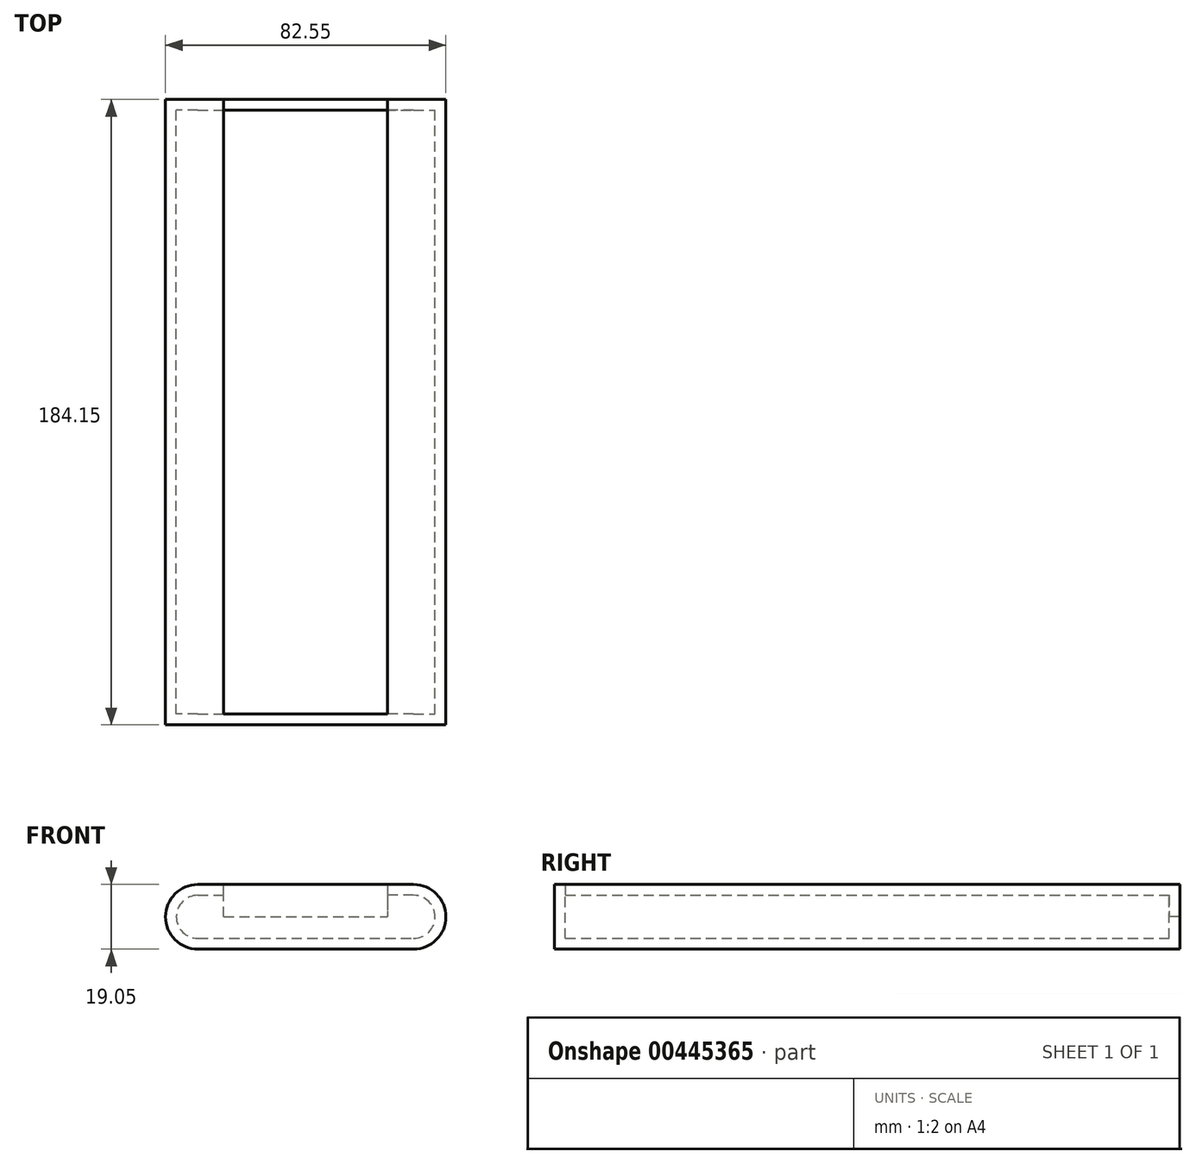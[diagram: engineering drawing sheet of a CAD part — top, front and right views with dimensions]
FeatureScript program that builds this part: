
annotation { "Feature Type Name" : "Feature", "Feature Type Description" : "" }
export const myFeature = defineFeature(function(context is Context, id is Id, definition is map)
    precondition{}
    {
        {
            var Q0;
            Q0=qCreatedBy(makeId("Front.planeOp"),FACE);
            var sketch = newSketch(context, id + "F0", { "sketchPlane" : qUnion([Q0])});
            skLineSegment(sketch, "E0", {"start": v(9.53, 0) * mm, "end": v(73.03, 0) * mm});
            skLineSegment(sketch, "E1", {"start": v(0, 9.53) * mm, "end": v(0, 9.53) * mm});
            skLineSegment(sketch, "E2", {"start": v(82.55, 9.53) * mm, "end": v(82.55, 9.53) * mm});
            skLineSegment(sketch, "E3", {"start": v(9.52, 19.05) * mm, "end": v(17.15, 19.05) * mm});
            skLineSegment(sketch, "E4", {"start": v(73.03, 19.05) * mm, "end": v(65.4, 19.05) * mm});
            skLineSegment(sketch, "E5.0", {"start": v(9.53, 3.18) * mm, "end": v(73.03, 3.18) * mm});
            skLineSegment(sketch, "E6.0", {"start": v(9.53, 15.88) * mm, "end": v(17.15, 15.88) * mm});
            skLineSegment(sketch, "E7.0", {"start": v(73.03, 15.88) * mm, "end": v(65.4, 15.88) * mm});
            skLineSegment(sketch, "E8", {"start": v(17.15, 15.88) * mm, "end": v(17.15, 19.05) * mm});
            skLineSegment(sketch, "E9", {"start": v(65.4, 19.05) * mm, "end": v(65.4, 15.87) * mm});
            skPoint(sketch, "E10.visualSharp", {"position": v(0, 19.05) * mm});
            skArc(sketch, "E10.filletArc", {"start": v(9.52, 19.05) * mm, "mid": v(2.79, 16.26) * mm, "end": v(0, 9.53) * mm});
            skPoint(sketch, "E11.visualSharp", {"position": v(0, 0) * mm});
            skArc(sketch, "E11.filletArc", {"start": v(0, 9.53) * mm, "mid": v(2.79, 2.79) * mm, "end": v(9.53, 0) * mm});
            skPoint(sketch, "E12.visualSharp", {"position": v(82.55, 19.05) * mm});
            skArc(sketch, "E12.filletArc", {"start": v(82.55, 9.53) * mm, "mid": v(79.76, 16.26) * mm, "end": v(73.03, 19.05) * mm});
            skPoint(sketch, "E13.visualSharp", {"position": v(82.55, 0) * mm});
            skArc(sketch, "E13.filletArc", {"start": v(73.03, 0) * mm, "mid": v(79.76, 2.79) * mm, "end": v(82.55, 9.53) * mm});
            skArc(sketch, "E14.0", {"start": v(79.38, 9.52) * mm, "mid": v(77.52, 14.02) * mm, "end": v(73.03, 15.87) * mm});
            skArc(sketch, "E15.0", {"start": v(73.03, 3.18) * mm, "mid": v(77.52, 5.03) * mm, "end": v(79.38, 9.53) * mm});
            skArc(sketch, "E16.0", {"start": v(9.53, 15.88) * mm, "mid": v(5.03, 14.02) * mm, "end": v(3.18, 9.53) * mm});
            skArc(sketch, "E17.0", {"start": v(3.18, 9.53) * mm, "mid": v(5.03, 5.03) * mm, "end": v(9.53, 3.18) * mm});
            skSolve(sketch);
        }
        {
            var Q0;
            Q0=makeQuery(id+"F0.imprint","IMPRINT",FACE,{"disambiguationData":[TD([[makeQuery(id+"F0.imprint","IMPRINT",EDGE,{"derivedFrom":sQuery(id+"F0.wireOp",EDGE,"E0")}),1.0]])]});
            extrude(context, id + "F1", {"entities" : qUnion([Q0]), "depth" : 177.8 * mm});
        }
        {
            var Q0;
            Q0=makeQuery(id+"F1.opExtrude","CAP_FACE",FACE,{"disambiguationData":[OSD([sQuery(id+"F0.wireOp",EDGE,"E0"),sQuery(id+"F0.wireOp",EDGE,"E3"),sQuery(id+"F0.wireOp",EDGE,"E4"),sQuery(id+"F0.wireOp",EDGE,"E5.0"),sQuery(id+"F0.wireOp",EDGE,"E6.0"),sQuery(id+"F0.wireOp",EDGE,"E7.0"),sQuery(id+"F0.wireOp",EDGE,"E8"),sQuery(id+"F0.wireOp",EDGE,"E9"),sQuery(id+"F0.wireOp",EDGE,"E10.filletArc"),sQuery(id+"F0.wireOp",EDGE,"E11.filletArc"),sQuery(id+"F0.wireOp",EDGE,"E12.filletArc"),sQuery(id+"F0.wireOp",EDGE,"E13.filletArc"),sQuery(id+"F0.wireOp",EDGE,"E14.0"),sQuery(id+"F0.wireOp",EDGE,"E15.0"),sQuery(id+"F0.wireOp",EDGE,"E16.0"),sQuery(id+"F0.wireOp",EDGE,"E17.0")])],"isStart":false});
            var sketch = newSketch(context, id + "F2", { "sketchPlane" : qUnion([Q0])});
            skLineSegment(sketch, "E18", {"start": v(9.52, 19.05) * mm, "end": v(73.03, 19.05) * mm});
            skLineSegment(sketch, "E19", {"start": v(73.03, 0) * mm, "end": v(9.52, 0) * mm});
            skLineSegment(sketch, "E20.0", {"start": v(0, 9.52) * mm, "end": v(0, 9.52) * mm});
            skPoint(sketch, "E21.visualSharp", {"position": v(0, 19.05) * mm});
            skArc(sketch, "E21.filletArc", {"start": v(9.52, 19.05) * mm, "mid": v(2.79, 16.26) * mm, "end": v(0, 9.52) * mm});
            skPoint(sketch, "E22.visualSharp", {"position": v(0, 0) * mm});
            skArc(sketch, "E22.filletArc", {"start": v(0, 9.52) * mm, "mid": v(2.79, 2.79) * mm, "end": v(9.53, 0) * mm});
            skLineSegment(sketch, "E23.0", {"start": v(82.55, 9.52) * mm, "end": v(82.55, 9.53) * mm});
            skArc(sketch, "E24.filletArc", {"start": v(82.55, 9.52) * mm, "mid": v(79.76, 16.26) * mm, "end": v(73.03, 19.05) * mm});
            skArc(sketch, "E25.filletArc", {"start": v(73.03, 0) * mm, "mid": v(79.76, 2.79) * mm, "end": v(82.55, 9.53) * mm});
            skSolve(sketch);
        }
        {
            var Q0;
            Q0 = qSketchRegion(id + "F2", true);
            extrude(context, id + "F3", {"entities" : qUnion([Q0]), "operationType" : NewBodyOperationType.ADD, "depth" : 3.17 * mm});
        }
        {
            var Q0;
            Q0=makeQuery(id+"F1.opExtrude","CAP_FACE",FACE,{"disambiguationData":[OSD([sQuery(id+"F0.wireOp",EDGE,"E0"),sQuery(id+"F0.wireOp",EDGE,"E3"),sQuery(id+"F0.wireOp",EDGE,"E4"),sQuery(id+"F0.wireOp",EDGE,"E5.0"),sQuery(id+"F0.wireOp",EDGE,"E6.0"),sQuery(id+"F0.wireOp",EDGE,"E7.0"),sQuery(id+"F0.wireOp",EDGE,"E8"),sQuery(id+"F0.wireOp",EDGE,"E9"),sQuery(id+"F0.wireOp",EDGE,"E10.filletArc"),sQuery(id+"F0.wireOp",EDGE,"E11.filletArc"),sQuery(id+"F0.wireOp",EDGE,"E12.filletArc"),sQuery(id+"F0.wireOp",EDGE,"E13.filletArc"),sQuery(id+"F0.wireOp",EDGE,"E14.0"),sQuery(id+"F0.wireOp",EDGE,"E15.0"),sQuery(id+"F0.wireOp",EDGE,"E16.0"),sQuery(id+"F0.wireOp",EDGE,"E17.0")])],"isStart":true});
            var sketch = newSketch(context, id + "F4", { "sketchPlane" : qUnion([Q0])});
            skLineSegment(sketch, "E26", {"start": v(-65.4, 19.05) * mm, "end": v(-65.4, 9.53) * mm});
            skPoint(sketch, "E26.endSnap0", {"position": v(-65.4, 17.46) * mm});
            skLineSegment(sketch, "E27", {"start": v(-17.15, 19.05) * mm, "end": v(-17.15, 9.53) * mm});
            skLineSegment(sketch, "E28", {"start": v(-17.15, 9.53) * mm, "end": v(-65.4, 9.53) * mm});
            skLineSegment(sketch, "E29", {"start": v(-76.83, 19.05) * mm, "end": v(-73.03, 19.05) * mm});
            skLineSegment(sketch, "E30", {"start": v(-17.15, 19.05) * mm, "end": v(-9.53, 19.05) * mm});
            skLineSegment(sketch, "E31", {"start": v(0, 9.53) * mm, "end": v(0, 9.53) * mm});
            skLineSegment(sketch, "E32", {"start": v(-9.52, 0) * mm, "end": v(-73.03, 0) * mm});
            skPoint(sketch, "E33.visualSharp", {"position": v(0, 19.05) * mm});
            skArc(sketch, "E33.filletArc", {"start": v(0, 9.53) * mm, "mid": v(-2.79, 16.26) * mm, "end": v(-9.52, 19.05) * mm});
            skPoint(sketch, "E34.visualSharp", {"position": v(0, 0) * mm});
            skArc(sketch, "E34.filletArc", {"start": v(-9.52, 0) * mm, "mid": v(-2.79, 2.79) * mm, "end": v(0, 9.53) * mm});
            skLineSegment(sketch, "E35", {"start": v(-82.55, 9.53) * mm, "end": v(-82.55, 9.52) * mm});
            skPoint(sketch, "E36.orphan", {"position": v(-82.55, 9.53) * mm});
            skPoint(sketch, "E37.visualSharp", {"position": v(-82.55, 19.05) * mm});
            skArc(sketch, "E37.filletArc", {"start": v(-73.03, 19.05) * mm, "mid": v(-79.76, 16.26) * mm, "end": v(-82.55, 9.52) * mm});
            skPoint(sketch, "E38.visualSharp", {"position": v(-82.55, 0) * mm});
            skArc(sketch, "E38.filletArc", {"start": v(-82.55, 9.53) * mm, "mid": v(-79.76, 2.79) * mm, "end": v(-73.03, 0) * mm});
            skLineSegment(sketch, "E39", {"start": v(-76.83, 19.05) * mm, "end": v(-65.4, 19.05) * mm});
            skSolve(sketch);
        }
        {
            var Q0;
            Q0 = qSketchRegion(id + "F4", true);
            extrude(context, id + "F5", {"entities" : qUnion([Q0]), "operationType" : NewBodyOperationType.ADD, "depth" : 3.17 * mm});
        }
    });
